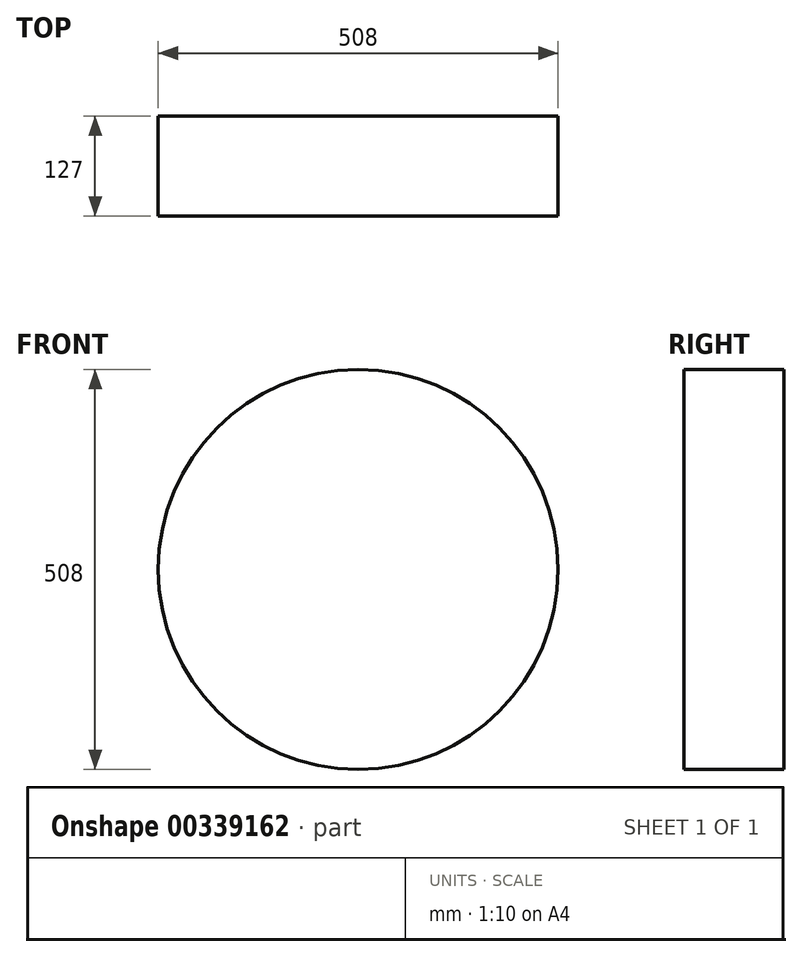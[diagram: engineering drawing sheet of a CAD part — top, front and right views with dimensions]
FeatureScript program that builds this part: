
annotation { "Feature Type Name" : "Feature", "Feature Type Description" : "" }
export const myFeature = defineFeature(function(context is Context, id is Id, definition is map)
    precondition{}
    {
        {
            var Q0;
            Q0=qCreatedBy(makeId("Front.planeOp"),FACE);
            var sketch = newSketch(context, id + "F0", { "sketchPlane" : qUnion([Q0])});
            skCircle(sketch, "E0", {"center": v(0, 0) * mm, "radius": 254 * mm});
            skSolve(sketch);
        }
        {
            var Q0;
            Q0 = qSketchRegion(id + "F0", true);
            extrude(context, id + "F1", {"entities" : qUnion([Q0]), "depth" : 127 * mm});
        }
    });
